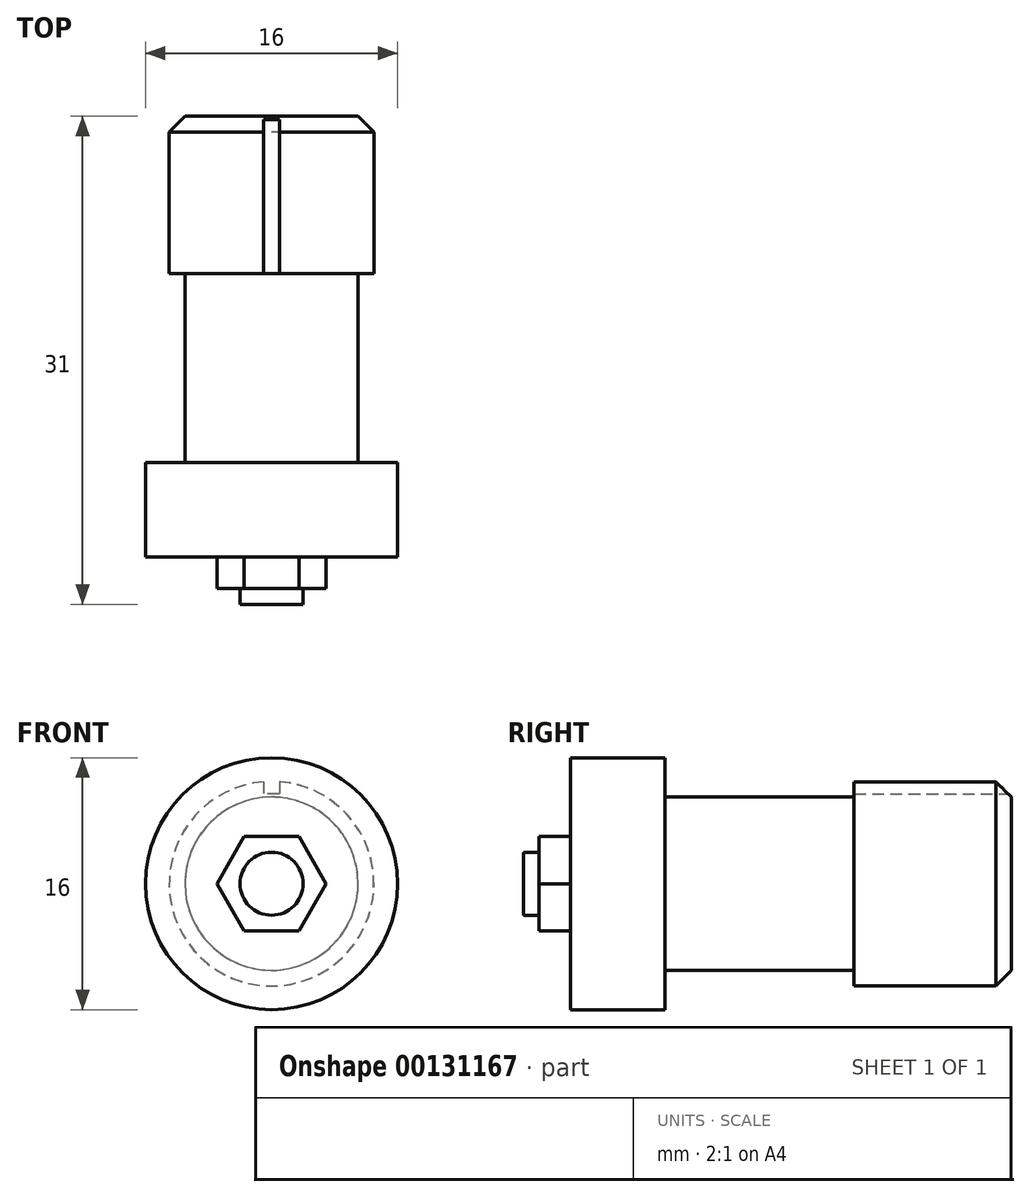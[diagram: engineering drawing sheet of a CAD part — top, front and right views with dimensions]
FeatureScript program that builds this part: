
annotation { "Feature Type Name" : "Feature", "Feature Type Description" : "" }
export const myFeature = defineFeature(function(context is Context, id is Id, definition is map)
    precondition{}
    {
        {
            var Q0;
            Q0=qCreatedBy(makeId("Front.planeOp"),FACE);
            var sketch = newSketch(context, id + "F0", { "sketchPlane" : qUnion([Q0])});
            skCircle(sketch, "E0", {"center": v(0, 0) * mm, "radius": 8 * mm});
            skSolve(sketch);
        }
        {
            var Q0;
            Q0=makeQuery(id+"F0.imprint","IMPRINT",FACE,{"disambiguationData":[TD([[makeQuery(id+"F0.imprint","IMPRINT",EDGE,{"derivedFrom":sQuery(id+"F0.wireOp",EDGE,"E0")}),1.0]])]});
            extrude(context, id + "F1", {"entities" : qUnion([Q0]), "oppositeDirection" : true, "depth" : 6 * mm});
        }
        {
            var Q0;
            Q0=makeQuery(id+"F1.opExtrude","CAP_FACE",FACE,{"disambiguationData":[OSD([sQuery(id+"F0.wireOp",EDGE,"E0")])],"isStart":true});
            var sketch = newSketch(context, id + "F2", { "sketchPlane" : qUnion([Q0])});
            skCircle(sketch, "E1.cCircle", {"center": v(0, 0) * mm, "radius": 3 * mm, "construction": true});
            skLineSegment(sketch, "E1.0", {"start": v(3.46, 0) * mm, "end": v(1.73, -3) * mm});
            skLineSegment(sketch, "E1.1", {"start": v(1.73, -3) * mm, "end": v(-1.73, -3) * mm});
            skLineSegment(sketch, "E1.2", {"start": v(-1.73, -3) * mm, "end": v(-3.46, 0) * mm});
            skLineSegment(sketch, "E1.3", {"start": v(-3.46, 0) * mm, "end": v(-1.73, 3) * mm});
            skLineSegment(sketch, "E1.4", {"start": v(-1.73, 3) * mm, "end": v(1.73, 3) * mm});
            skLineSegment(sketch, "E1.5", {"start": v(1.73, 3) * mm, "end": v(3.46, 0) * mm});
            skPoint(sketch, "E1.0.midPoint", {"position": v(2.6, -1.5) * mm});
            skSolve(sketch);
        }
        {
            var Q0;
            Q0=makeQuery(id+"F2.imprint","IMPRINT",FACE,{"disambiguationData":[TD([[makeQuery(id+"F2.imprint","IMPRINT",EDGE,{"derivedFrom":sQuery(id+"F2.wireOp",EDGE,"E1.0")}),-1.0]])]});
            extrude(context, id + "F3", {"entities" : qUnion([Q0]), "operationType" : NewBodyOperationType.ADD, "depth" : 2 * mm});
        }
        {
            var Q0;
            Q0=makeQuery(id+"F3.opExtrude","CAP_FACE",FACE,{"disambiguationData":[OSD([sQuery(id+"F2.wireOp",EDGE,"E1.0"),sQuery(id+"F2.wireOp",EDGE,"E1.1"),sQuery(id+"F2.wireOp",EDGE,"E1.2"),sQuery(id+"F2.wireOp",EDGE,"E1.3"),sQuery(id+"F2.wireOp",EDGE,"E1.4"),sQuery(id+"F2.wireOp",EDGE,"E1.5")])],"isStart":false});
            var sketch = newSketch(context, id + "F4", { "sketchPlane" : qUnion([Q0])});
            skCircle(sketch, "E2", {"center": v(0, 0) * mm, "radius": 2 * mm});
            skSolve(sketch);
        }
        {
            var Q0;
            Q0=makeQuery(id+"F4.imprint","IMPRINT",FACE,{"disambiguationData":[TD([[makeQuery(id+"F4.imprint","IMPRINT",EDGE,{"derivedFrom":sQuery(id+"F4.wireOp",EDGE,"E2")}),1.0]])]});
            extrude(context, id + "F5", {"entities" : qUnion([Q0]), "operationType" : NewBodyOperationType.ADD, "depth" : 1 * mm});
        }
        {
            var Q0;
            Q0=makeQuery(id+"F1.opExtrude","CAP_FACE",FACE,{"disambiguationData":[OSD([sQuery(id+"F0.wireOp",EDGE,"E0")])],"isStart":false});
            var sketch = newSketch(context, id + "F6", { "sketchPlane" : qUnion([Q0])});
            skCircle(sketch, "E3", {"center": v(0, 0) * mm, "radius": 5.5 * mm});
            skSolve(sketch);
        }
        {
            var Q0;
            Q0=makeQuery(id+"F6.imprint","IMPRINT",FACE,{"disambiguationData":[TD([[makeQuery(id+"F6.imprint","IMPRINT",EDGE,{"derivedFrom":sQuery(id+"F6.wireOp",EDGE,"E3")}),1.0]])]});
            extrude(context, id + "F7", {"entities" : qUnion([Q0]), "operationType" : NewBodyOperationType.ADD, "depth" : 22 * mm});
        }
        {
            var Q0;
            Q0=makeQuery(id+"F7.opExtrude","CAP_FACE",FACE,{"disambiguationData":[OSD([sQuery(id+"F6.wireOp",EDGE,"E3")])],"isStart":false});
            var sketch = newSketch(context, id + "F8", { "sketchPlane" : qUnion([Q0])});
            skCircle(sketch, "E4", {"center": v(0, 0) * mm, "radius": 6.5 * mm});
            skSolve(sketch);
        }
        {
            var Q0;
            Q0=makeQuery(id+"F8.imprint","IMPRINT",FACE,{"disambiguationData":[TD([[makeQuery(id+"F8.imprint","IMPRINT",EDGE,{"derivedFrom":sQuery(id+"F8.wireOp",EDGE,"E4")}),1.0]])]});
            extrude(context, id + "F9", {"entities" : qUnion([Q0]), "operationType" : NewBodyOperationType.ADD, "oppositeDirection" : true, "depth" : 10 * mm});
        }
        {
            var Q0;
            Q0=makeQuery(id+"F9.opExtrude","CAP_EDGE",EDGE,{"disambiguationData":[OSD([sQuery(id+"F8.wireOp",EDGE,"E4")])],"isStart":true});
            chamfer(context, id + "F10", {"entities" : qUnion([Q0]), "width" : 1 * mm, "tangentPropagation" : true});
        }
        {
            var Q0;
            {var subQ0=sQuery(id+"F6.wireOp",EDGE,"E3");Q0=makeQuery(id+"F9.boolean.opBoolean","MERGE",FACE,{"derivedFrom":[makeQuery(id+"F7.opExtrude","CAP_FACE",FACE,{"disambiguationData":[OSD([subQ0])],"isStart":false}),makeQuery(id+"F9.opExtrude","CAP_FACE",FACE,{"disambiguationData":[OSD([subQ0,sQuery(id+"F8.wireOp",EDGE,"E4")])],"isStart":true})]});}
            var sketch = newSketch(context, id + "F11", { "sketchPlane" : qUnion([Q0])});
            skLineSegment(sketch, "E5.bottom", {"start": v(-0.5, 7.7) * mm, "end": v(0.5, 7.7) * mm});
            skLineSegment(sketch, "E5.top", {"start": v(-0.5, 5.7) * mm, "end": v(0.5, 5.7) * mm});
            skLineSegment(sketch, "E5.left", {"start": v(-0.5, 7.7) * mm, "end": v(-0.5, 5.7) * mm});
            skLineSegment(sketch, "E5.right", {"start": v(0.5, 7.7) * mm, "end": v(0.5, 5.7) * mm});
            skLineSegment(sketch, "E6", {"start": v(0, 5.7) * mm, "end": v(0, 0) * mm, "construction": true});
            skSolve(sketch);
        }
        {
            var Q0;
            Q0=makeQuery(id+"F11.imprint","IMPRINT",FACE,{"disambiguationData":[TD([[makeQuery(id+"F11.imprint","IMPRINT",EDGE,{"derivedFrom":sQuery(id+"F11.wireOp",EDGE,"E5.bottom")}),-1.0]])]});
            extrude(context, id + "F12", {"entities" : qUnion([Q0]), "operationType" : NewBodyOperationType.REMOVE, "oppositeDirection" : true, "depth" : 20 * mm});
        }
    });
